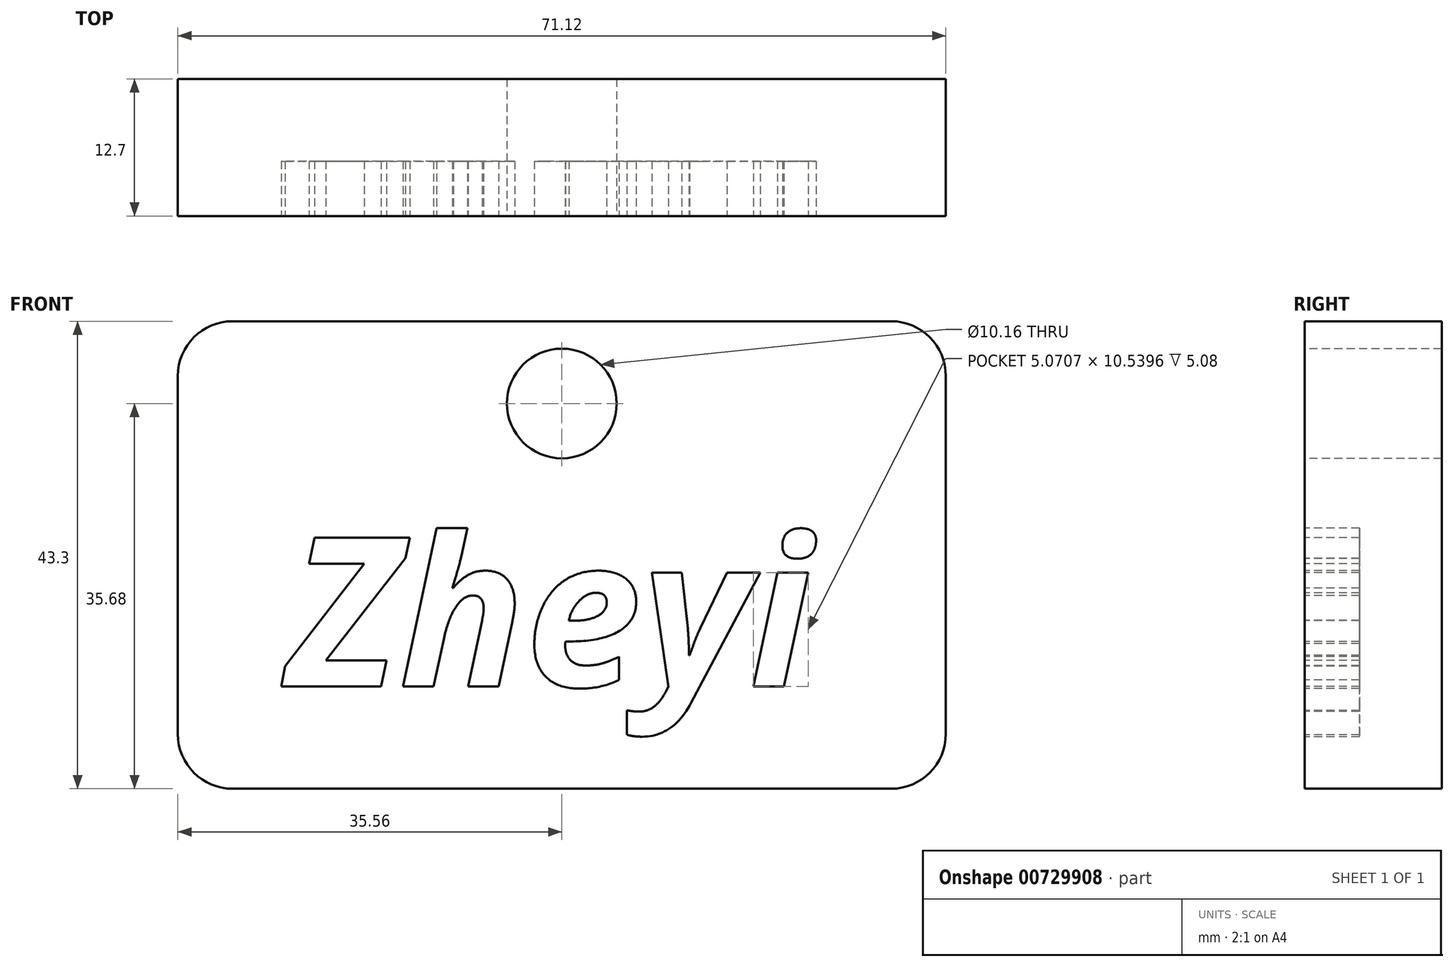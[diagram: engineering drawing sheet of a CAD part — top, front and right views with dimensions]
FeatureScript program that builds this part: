
annotation { "Feature Type Name" : "Feature", "Feature Type Description" : "" }
export const myFeature = defineFeature(function(context is Context, id is Id, definition is map)
    precondition{}
    {
        {
            var Q0;
            Q0=qCreatedBy(makeId("Front.planeOp"),FACE);
            var sketch = newSketch(context, id + "F0", { "sketchPlane" : qUnion([Q0])});
            skLineSegment(sketch, "E0.bottom", {"start": v(-35.56, 21.65) * mm, "end": v(35.56, 21.65) * mm});
            skLineSegment(sketch, "E0.top", {"start": v(-35.56, -21.65) * mm, "end": v(35.56, -21.65) * mm});
            skLineSegment(sketch, "E0.left", {"start": v(-35.56, 21.65) * mm, "end": v(-35.56, -21.65) * mm});
            skLineSegment(sketch, "E0.right", {"start": v(35.56, 21.65) * mm, "end": v(35.56, -21.65) * mm});
            skSolve(sketch);
        }
        {
            var Q0;
            Q0=makeQuery(id+"F0.imprint","IMPRINT",FACE,{"disambiguationData":[TD([[makeQuery(id+"F0.imprint","IMPRINT",EDGE,{"derivedFrom":sQuery(id+"F0.wireOp",EDGE,"E0.bottom")}),-1.0]])]});
            extrude(context, id + "F1", {"entities" : qUnion([Q0]), "depth" : 12.7 * mm, "offsetDistance" : 25.4 * mm});
        }
        {
            var Q0;
            Q0=makeQuery(id+"F1.opExtrude","CAP_FACE",FACE,{"disambiguationData":[OSD([sQuery(id+"F0.wireOp",EDGE,"E0.bottom"),sQuery(id+"F0.wireOp",EDGE,"E0.top"),sQuery(id+"F0.wireOp",EDGE,"E0.left"),sQuery(id+"F0.wireOp",EDGE,"E0.right")])],"isStart":false});
            var sketch = newSketch(context, id + "F2", { "sketchPlane" : qUnion([Q0])});
            skText(sketch, "E1", { "text": "Zheyi", "fontName": "OpenSans-BoldItalic.ttf"});
            const initialGuessF2  = {"E1": [-0.0254, -0.01219, 1, 0, 0.0139]};
            skSetInitialGuess(sketch, initialGuessF2);
            skSolve(sketch);
        }
        {
            var Q0;
            Q0 = qSketchRegion(id + "F2", true);
            extrude(context, id + "F3", {"entities" : qUnion([Q0]), "operationType" : NewBodyOperationType.REMOVE, "oppositeDirection" : true, "depth" : 5.08 * mm, "offsetDistance" : 25.4 * mm});
        }
        {
            var Q0;
            {var subQ0=sQuery(id+"F0.wireOp",EDGE,"E0.left");var subQ1=sQuery(id+"F0.wireOp",EDGE,"E0.bottom");var subQ2=sQuery(id+"F0.wireOp",EDGE,"E0.right");var subQ3=sQuery(id+"F0.wireOp",EDGE,"E0.top");Q0=makeQuery(id+"F3.boolean.opBoolean","SPLIT",FACE,{"disambiguationData":[TD([makeQuery(id+"F1.opExtrude","SWEPT_FACE",FACE,{"disambiguationData":[OSD([subQ1])]})])],"derivedFrom":makeQuery(id+"F1.opExtrude","CAP_FACE",FACE,{"disambiguationData":[OSD([subQ1,subQ3,subQ0,subQ2])],"isStart":false})});}
            var sketch = newSketch(context, id + "F4", { "sketchPlane" : qUnion([Q0])});
            skCircle(sketch, "E2", {"center": v(0, 14.03) * mm, "radius": 5.08 * mm});
            skLineSegment(sketch, "E3", {"start": v(0, 14.03) * mm, "end": v(0, 21.65) * mm});
            skSolve(sketch);
        }
        {
            var Q0;
            Q0=makeQuery(id+"F4.imprint","IMPRINT",FACE,{"disambiguationData":[TD([[makeQuery(id+"F4.imprint","IMPRINT",EDGE,{"derivedFrom":sQuery(id+"F4.wireOp",EDGE,"E2")}),1.0]])]});
            extrude(context, id + "F5", {"entities" : qUnion([Q0]), "operationType" : NewBodyOperationType.REMOVE, "endBound" : BoundingType.THROUGH_ALL, "oppositeDirection" : true, "depth" : 25.4 * mm, "offsetDistance" : 25.4 * mm});
        }
        {
            var Q0;
            Q0=makeQuery(id+"F1.opExtrude","SWEPT_EDGE",EDGE,{"disambiguationData":[OSD([sQuery(id+"F0.wireOp",EDGE,"E0.bottom"),sQuery(id+"F0.wireOp",EDGE,"E0.right")])]});
            var Q1;
            Q1=makeQuery(id+"F1.opExtrude","SWEPT_EDGE",EDGE,{"disambiguationData":[OSD([sQuery(id+"F0.wireOp",EDGE,"E0.bottom"),sQuery(id+"F0.wireOp",EDGE,"E0.left")])]});
            var Q2;
            Q2=makeQuery(id+"F1.opExtrude","SWEPT_EDGE",EDGE,{"disambiguationData":[OSD([sQuery(id+"F0.wireOp",EDGE,"E0.top"),sQuery(id+"F0.wireOp",EDGE,"E0.right")])]});
            var Q3;
            Q3=makeQuery(id+"F1.opExtrude","SWEPT_EDGE",EDGE,{"disambiguationData":[OSD([sQuery(id+"F0.wireOp",EDGE,"E0.top"),sQuery(id+"F0.wireOp",EDGE,"E0.left")])]});
            fillet(context, id + "F6", {"entities" : qUnion([Q0, Q1, Q2, Q3]), "radius" : 5.08 * mm, "tangentPropagation" : true, "allowEdgeOverflow" : false});
        }
    });
